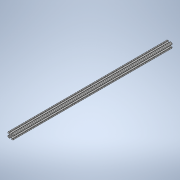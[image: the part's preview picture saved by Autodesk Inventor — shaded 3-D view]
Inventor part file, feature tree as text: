
AUTODESK INVENTOR PART (.ipt)
format: ipt  version: 2020 (Build 240168000, 168)  size: 236,032 bytes
history: native  units: in
note: dims shown in document units (in); Inventor stores cm internally (conversion verified against a paired STEP export)
features: extrude x1, sketch x1
ambient origin geometry x8: Origin, YZ Plane, XZ Plane, XY Plane, X Axis, Y Axis, Z Axis, Center Point
bodies: Solid1 (feature_tree)
feature tree (2):
  extrude  "Extrusion1"  [1 undecoded]
  sketch  "Sketch1"  dims[d0=30.0in d1=0.0in]
note: 1 required parameter value undecoded (feature->parameter linkage not recoverable at this tier; creation-order binding heuristic only, values carry confidence <= 0.55)
